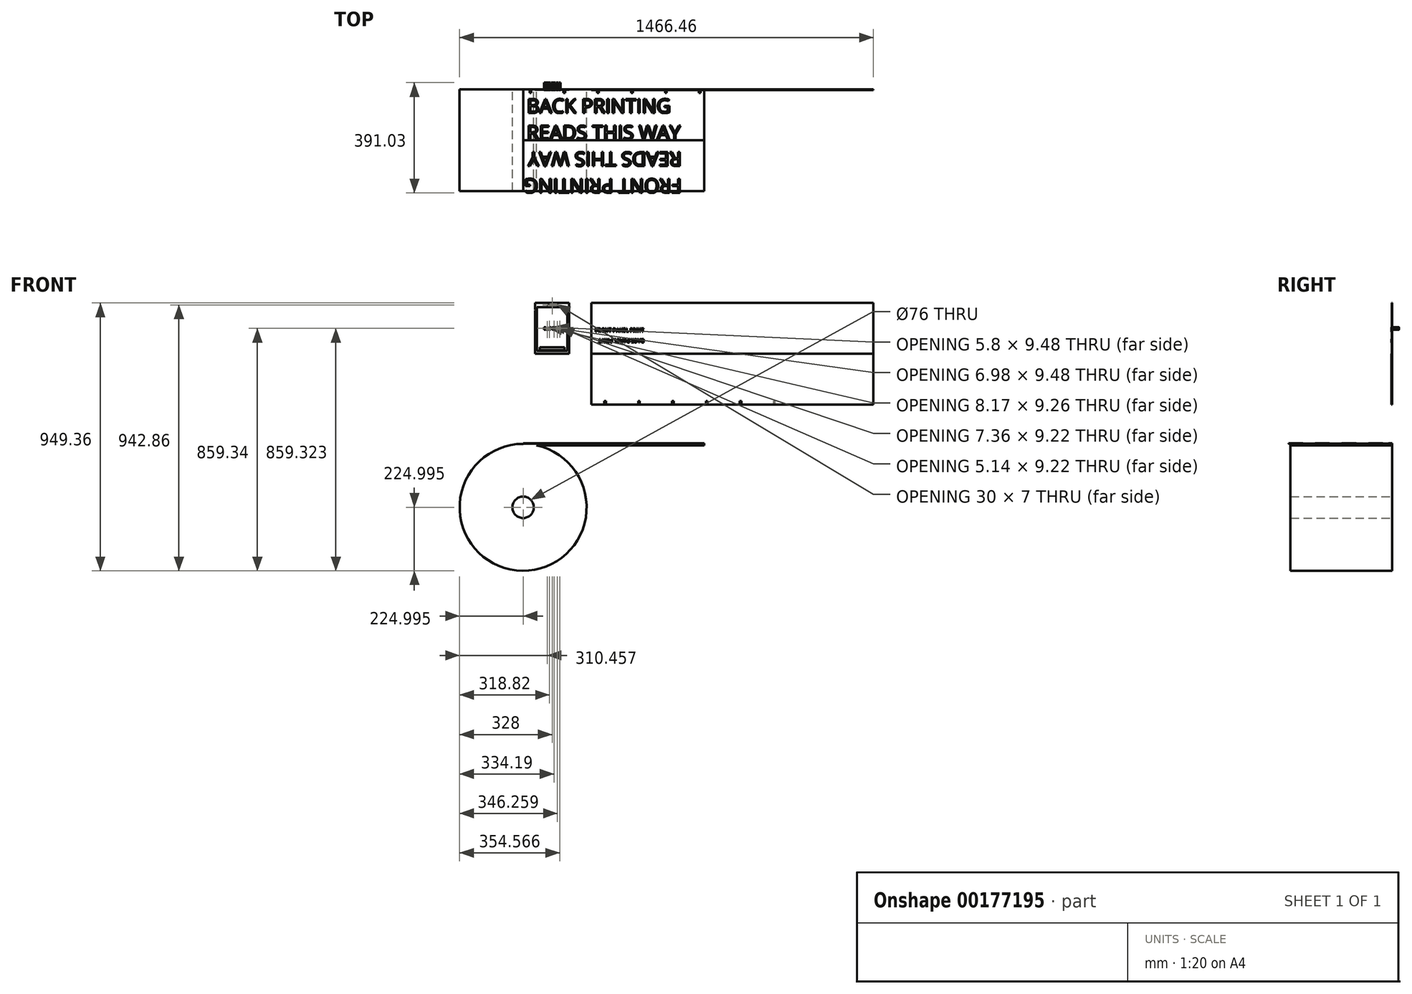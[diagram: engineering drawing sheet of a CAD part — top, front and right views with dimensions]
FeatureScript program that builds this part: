
annotation { "Feature Type Name" : "Feature", "Feature Type Description" : "" }
export const myFeature = defineFeature(function(context is Context, id is Id, definition is map)
    precondition{}
    {
        {
            assignVariable(context, id + "F0", {"name" : "hoogte", "anyValue" : 180});
        }
        {
            var Q0;
            Q0=qCreatedBy(makeId("Front.planeOp"),FACE);
            var sketch = newSketch(context, id + "F1", { "sketchPlane" : qUnion([Q0])});
            skLineSegment(sketch, "E0.bottom", {"start": v(-60, 90) * mm, "end": v(60, 90) * mm});
            skLineSegment(sketch, "E0.top", {"start": v(-60, -90) * mm, "end": v(60, -90) * mm});
            skLineSegment(sketch, "E0.left", {"start": v(-60, 90) * mm, "end": v(-60, -90) * mm});
            skLineSegment(sketch, "E0.right", {"start": v(60, 90) * mm, "end": v(60, -90) * mm});
            skLineSegment(sketch, "E1", {"start": v(-60, 66.41) * mm, "end": v(-58.59, 65) * mm});
            skLineSegment(sketch, "E2", {"start": v(-58.59, 65) * mm, "end": v(-60, 63.59) * mm});
            skLineSegment(sketch, "E3", {"start": v(60, 66.41) * mm, "end": v(58.59, 65) * mm});
            skLineSegment(sketch, "E4", {"start": v(58.59, 65) * mm, "end": v(60, 63.59) * mm});
            skLineSegment(sketch, "E5.bottom", {"start": v(138.46, 90) * mm, "end": v(1138.46, 90) * mm});
            skLineSegment(sketch, "E5.top", {"start": v(138.46, -270) * mm, "end": v(1138.46, -270) * mm});
            skLineSegment(sketch, "E5.left", {"start": v(138.46, 90) * mm, "end": v(138.46, -270) * mm});
            skLineSegment(sketch, "E5.right", {"start": v(1138.46, 90) * mm, "end": v(1138.46, -270) * mm});
            skLineSegment(sketch, "E6", {"start": v(138.46, -90) * mm, "end": v(1138.46, -90) * mm});
            skLineSegment(sketch, "E7", {"start": v(-60, 90) * mm, "end": v(60, -90) * mm, "construction": true});
            skLineSegment(sketch, "E8", {"start": v(60, 90) * mm, "end": v(-60, -90) * mm, "construction": true});
            skPoint(sketch, "E9", {"position": v(0, 0) * mm});
            skSolve(sketch);
        }
        {
            var Q0;
            {var subQ3=sQuery(id+"F1.wireOp",EDGE,"E0.bottom");Q0=makeQuery(id+"F1.imprint","IMPRINT",FACE,{"disambiguationData":[TD([[makeQuery(id+"F1.imprint","IMPRINT",EDGE,{"derivedFrom":subQ3}),-1.0]])]});}
            var Q1;
            Q1=makeQuery(id+"F1.imprint","IMPRINT",FACE,{"disambiguationData":[TD([[makeQuery(id+"F1.imprint","IMPRINT",EDGE,{"derivedFrom":sQuery(id+"F1.wireOp",EDGE,"E5.bottom")}),-1.0]])]});
            var Q2;
            {var subQ0=sQuery(id+"F1.wireOp",EDGE,"E5.top");Q2=makeQuery(id+"F1.imprint","IMPRINT",FACE,{"disambiguationData":[TD([[makeQuery(id+"F1.imprint","IMPRINT",EDGE,{"derivedFrom":subQ0}),1.0]])]});}
            extrude(context, id + "F2", {"entities" : qUnion([Q0, Q1, Q2]), "depth" : 1 * mm});
        }
        {
            var Q0;
            Q0=makeQuery(id+"F2.opExtrude","CAP_FACE",FACE,{"disambiguationData":[OSD([sQuery(id+"F1.wireOp",EDGE,"E0.bottom"),sQuery(id+"F1.wireOp",EDGE,"E0.top"),sQuery(id+"F1.wireOp",EDGE,"E0.left"),sQuery(id+"F1.wireOp",EDGE,"E0.right"),sQuery(id+"F1.wireOp",EDGE,"E1"),sQuery(id+"F1.wireOp",EDGE,"E2"),sQuery(id+"F1.wireOp",EDGE,"E3"),sQuery(id+"F1.wireOp",EDGE,"E4")])],"isStart":false});
            var sketch = newSketch(context, id + "F3", { "sketchPlane" : qUnion([Q0])});
            skLineSegment(sketch, "E10.0.0", {"start": v(60, 90) * mm, "end": v(-60, 90) * mm});
            skLineSegment(sketch, "E10.0.1", {"start": v(-60, 90) * mm, "end": v(-60, 66.41) * mm});
            skLineSegment(sketch, "E10.0.2", {"start": v(-60, 66.41) * mm, "end": v(-58.59, 65) * mm});
            skLineSegment(sketch, "E10.0.3", {"start": v(-58.59, 65) * mm, "end": v(-60, 63.59) * mm});
            skLineSegment(sketch, "E10.0.4", {"start": v(-60, 63.59) * mm, "end": v(-60, -90) * mm});
            skLineSegment(sketch, "E10.0.5", {"start": v(-60, -90) * mm, "end": v(60, -90) * mm});
            skLineSegment(sketch, "E10.0.6", {"start": v(60, -90) * mm, "end": v(60, 63.59) * mm});
            skLineSegment(sketch, "E10.0.7", {"start": v(60, 63.59) * mm, "end": v(58.59, 65) * mm});
            skLineSegment(sketch, "E10.0.8", {"start": v(58.59, 65) * mm, "end": v(60, 66.41) * mm});
            skLineSegment(sketch, "E10.0.9", {"start": v(60, 66.41) * mm, "end": v(60, 90) * mm});
            skLineSegment(sketch, "E11.bottom", {"start": v(-54, 75) * mm, "end": v(54, 75) * mm});
            skLineSegment(sketch, "E11.top", {"start": v(-54, -80) * mm, "end": v(54, -80) * mm});
            skLineSegment(sketch, "E11.left", {"start": v(-54, 75) * mm, "end": v(-54, -80) * mm});
            skLineSegment(sketch, "E11.right", {"start": v(54, 75) * mm, "end": v(54, -80) * mm});
            skLineSegment(sketch, "E12.bottom", {"start": v(-60, 90) * mm, "end": v(-57, 90) * mm});
            skLineSegment(sketch, "E12.top", {"start": v(-60, 78) * mm, "end": v(-57, 78) * mm});
            skLineSegment(sketch, "E12.left", {"start": v(-60, 90) * mm, "end": v(-60, 78) * mm});
            skLineSegment(sketch, "E12.right", {"start": v(-57, 90) * mm, "end": v(-57, 78) * mm});
            skLineSegment(sketch, "E13.bottom", {"start": v(60, 90) * mm, "end": v(57, 90) * mm});
            skLineSegment(sketch, "E13.top", {"start": v(60, 78) * mm, "end": v(57, 78) * mm});
            skLineSegment(sketch, "E13.left", {"start": v(60, 90) * mm, "end": v(60, 78) * mm});
            skLineSegment(sketch, "E13.right", {"start": v(57, 90) * mm, "end": v(57, 78) * mm});
            skLineSegment(sketch, "E14.bottom", {"start": v(-44, -67) * mm, "end": v(44, -67) * mm});
            skLineSegment(sketch, "E14.top", {"start": v(-44, -77) * mm, "end": v(44, -77) * mm});
            skLineSegment(sketch, "E14.left", {"start": v(-44, -67) * mm, "end": v(-44, -77) * mm});
            skLineSegment(sketch, "E14.right", {"start": v(44, -67) * mm, "end": v(44, -77) * mm});
            skSolve(sketch);
        }
        {
            var Q0;
            Q0=makeQuery(id+"F3.imprint","IMPRINT",FACE,{"disambiguationData":[TD([[makeQuery(id+"F3.imprint","IMPRINT",EDGE,{"derivedFrom":sQuery(id+"F3.wireOp",EDGE,"E11.bottom")}),-1.0]])]});
            var Q1;
            Q1=makeQuery(id+"F3.imprint","IMPRINT",FACE,{"disambiguationData":[TD([[makeQuery(id+"F3.imprint","IMPRINT",EDGE,{"derivedFrom":sQuery(id+"F3.wireOp",EDGE,"E12.bottom")}),-1.0]])]});
            var Q2;
            Q2=makeQuery(id+"F3.imprint","IMPRINT",FACE,{"disambiguationData":[TD([[makeQuery(id+"F3.imprint","IMPRINT",EDGE,{"derivedFrom":sQuery(id+"F3.wireOp",EDGE,"E13.bottom")}),-1.0]])]});
            extrude(context, id + "F4", {"entities" : qUnion([Q0, Q1, Q2]), "operationType" : NewBodyOperationType.REMOVE, "oppositeDirection" : true, "depth" : 0.5 * mm});
        }
        {
            var Q0;
            Q0=makeQuery(id+"F2.opExtrude","CAP_FACE",FACE,{"disambiguationData":[OSD([sQuery(id+"F1.wireOp",EDGE,"E5.bottom"),sQuery(id+"F1.wireOp",EDGE,"E5.left"),sQuery(id+"F1.wireOp",EDGE,"E5.right"),sQuery(id+"F1.wireOp",EDGE,"E6")])],"isStart":false});
            var sketch = newSketch(context, id + "F5", { "sketchPlane" : qUnion([Q0])});
            skLineSegment(sketch, "E15.0.0", {"start": v(1138.46, 90) * mm, "end": v(138.46, 90) * mm});
            skLineSegment(sketch, "E15.0.1", {"start": v(138.46, 90) * mm, "end": v(138.46, 90) * mm});
            skLineSegment(sketch, "E15.0.2", {"start": v(138.46, 90) * mm, "end": v(1138.46, 90) * mm});
            skLineSegment(sketch, "E15.0.3", {"start": v(1138.46, 90) * mm, "end": v(1138.46, 90) * mm});
            skLineSegment(sketch, "E16.bottom", {"start": v(184.68, -270) * mm, "end": v(190.68, -270) * mm});
            skLineSegment(sketch, "E16.top", {"start": v(184.68, -258) * mm, "end": v(190.68, -258) * mm});
            skLineSegment(sketch, "E16.left", {"start": v(184.68, -270) * mm, "end": v(184.68, -258) * mm});
            skLineSegment(sketch, "E16.right", {"start": v(190.68, -270) * mm, "end": v(190.68, -258) * mm});
            skLineSegment(sketch, "E17.1.0.0", {"start": v(304.68, -258) * mm, "end": v(310.68, -258) * mm});
            skLineSegment(sketch, "E17.1.0.1", {"start": v(304.68, -270) * mm, "end": v(304.68, -258) * mm});
            skLineSegment(sketch, "E17.1.0.2", {"start": v(304.68, -270) * mm, "end": v(310.68, -270) * mm});
            skLineSegment(sketch, "E17.1.0.3", {"start": v(310.68, -270) * mm, "end": v(310.68, -258) * mm});
            skLineSegment(sketch, "E17.2.0.0", {"start": v(424.68, -258) * mm, "end": v(430.68, -258) * mm});
            skLineSegment(sketch, "E17.2.0.1", {"start": v(424.68, -270) * mm, "end": v(424.68, -258) * mm});
            skLineSegment(sketch, "E17.2.0.2", {"start": v(424.68, -270) * mm, "end": v(430.68, -270) * mm});
            skLineSegment(sketch, "E17.2.0.3", {"start": v(430.68, -270) * mm, "end": v(430.68, -258) * mm});
            skLineSegment(sketch, "E17.direction1", {"start": v(184.68, -270) * mm, "end": v(304.68, -270) * mm, "construction": true});
            skLineSegment(sketch, "E18.0.3.0", {"start": v(544.68, -258) * mm, "end": v(550.68, -258) * mm});
            skLineSegment(sketch, "E18.3.3.0", {"start": v(544.68, -270) * mm, "end": v(544.68, -258) * mm});
            skLineSegment(sketch, "E18.6.3.0", {"start": v(544.68, -270) * mm, "end": v(550.68, -270) * mm});
            skLineSegment(sketch, "E18.9.3.0", {"start": v(550.68, -270) * mm, "end": v(550.68, -258) * mm});
            skLineSegment(sketch, "E18.0.4.0", {"start": v(664.68, -258) * mm, "end": v(670.68, -258) * mm});
            skLineSegment(sketch, "E18.3.4.0", {"start": v(664.68, -270) * mm, "end": v(664.68, -258) * mm});
            skLineSegment(sketch, "E18.6.4.0", {"start": v(664.68, -270) * mm, "end": v(670.68, -270) * mm});
            skLineSegment(sketch, "E18.9.4.0", {"start": v(670.68, -270) * mm, "end": v(670.68, -258) * mm});
            skLineSegment(sketch, "E19.0.5.0", {"start": v(784.68, -258) * mm, "end": v(790.68, -258) * mm});
            skLineSegment(sketch, "E19.3.5.0", {"start": v(784.68, -270) * mm, "end": v(784.68, -258) * mm});
            skLineSegment(sketch, "E19.6.5.0", {"start": v(784.68, -270) * mm, "end": v(790.68, -270) * mm});
            skLineSegment(sketch, "E19.9.5.0", {"start": v(790.68, -270) * mm, "end": v(790.68, -258) * mm});
            skSolve(sketch);
        }
        {
            var Q0;
            Q0=makeQuery(id+"F5.imprint","IMPRINT",FACE,{"disambiguationData":[TD([[makeQuery(id+"F5.imprint","IMPRINT",EDGE,{"derivedFrom":sQuery(id+"F5.wireOp",EDGE,"JLQzprwf-iRJq-cmRX-vWmS-HmgRmsplr5sc.top")}),-1.0]])]});
            var Q1;
            Q1=makeQuery(id+"F5.imprint","IMPRINT",FACE,{"disambiguationData":[TD([[makeQuery(id+"F5.imprint","IMPRINT",EDGE,{"derivedFrom":sQuery(id+"F5.wireOp",EDGE,"E16.bottom")}),1.0]])]});
            var Q2;
            Q2=makeQuery(id+"F5.imprint","IMPRINT",FACE,{"disambiguationData":[TD([[makeQuery(id+"F5.imprint","IMPRINT",EDGE,{"derivedFrom":sQuery(id+"F5.wireOp",EDGE,"E17.1.0.0")}),-1.0]])]});
            var Q3;
            Q3=makeQuery(id+"F5.imprint","IMPRINT",FACE,{"disambiguationData":[TD([[makeQuery(id+"F5.imprint","IMPRINT",EDGE,{"derivedFrom":sQuery(id+"F5.wireOp",EDGE,"E17.2.0.0")}),-1.0]])]});
            var Q4;
            Q4=makeQuery(id+"F5.imprint","IMPRINT",FACE,{"disambiguationData":[TD([[makeQuery(id+"F5.imprint","IMPRINT",EDGE,{"derivedFrom":sQuery(id+"F5.wireOp",EDGE,"E18.0.3.0")}),-1.0]])]});
            var Q5;
            Q5=makeQuery(id+"F5.imprint","IMPRINT",FACE,{"disambiguationData":[TD([[makeQuery(id+"F5.imprint","IMPRINT",EDGE,{"derivedFrom":sQuery(id+"F5.wireOp",EDGE,"E18.0.4.0")}),-1.0]])]});
            var Q6;
            Q6=makeQuery(id+"F5.imprint","IMPRINT",FACE,{"disambiguationData":[TD([[makeQuery(id+"F5.imprint","IMPRINT",EDGE,{"derivedFrom":sQuery(id+"F5.wireOp",EDGE,"E19.0.5.0")}),-1.0]])]});
            extrude(context, id + "F6", {"entities" : qUnion([Q0, Q1, Q2, Q3, Q4, Q5, Q6]), "operationType" : NewBodyOperationType.REMOVE, "oppositeDirection" : true, "depth" : 0.5 * mm});
        }
        {
            var Q0;
            Q0=qCreatedBy(makeId("Front.planeOp"),FACE);
            var sketch = newSketch(context, id + "F7", { "sketchPlane" : qUnion([Q0])});
            skCircle(sketch, "E20", {"center": v(-103, -634.36) * mm, "radius": 225 * mm});
            skLineSegment(sketch, "E21.bottom", {"start": v(-103, -408.35) * mm, "end": v(538.87, -408.35) * mm});
            skLineSegment(sketch, "E21.top", {"start": v(-103, -414.51) * mm, "end": v(538.87, -414.51) * mm});
            skLineSegment(sketch, "E21.left", {"start": v(-103, -414.51) * mm, "end": v(-103, -408.35) * mm});
            skLineSegment(sketch, "E21.right", {"start": v(538.87, -414.51) * mm, "end": v(538.87, -408.35) * mm});
            skCircle(sketch, "E22", {"center": v(-103, -634.36) * mm, "radius": 38 * mm});
            skSolve(sketch);
        }
        {
            var Q0;
            Q0=qSketchRegion(id+"F7",true);
            extrude(context, id + "F8", {"entities" : qUnion([Q0]), "depth" : (((getVariable(context, 'hoogte')) * 2)) * mm});
        }
        {
            var Q0;
            {var subQ0=sQuery(id+"F1.wireOp",EDGE,"E4");var subQ1=sQuery(id+"F1.wireOp",EDGE,"E2");var subQ2=sQuery(id+"F1.wireOp",EDGE,"E1");var subQ3=sQuery(id+"F1.wireOp",EDGE,"E0.right");var subQ4=sQuery(id+"F1.wireOp",EDGE,"E0.top");var subQ5=sQuery(id+"F1.wireOp",EDGE,"E0.bottom");var subQ6=sQuery(id+"F1.wireOp",EDGE,"E3");var subQ7=sQuery(id+"F1.wireOp",EDGE,"E0.left");Q0=makeQuery(id+"F4.boolean.opBoolean","SPLIT",FACE,{"disambiguationData":[TD([makeQuery(id+"F2.opExtrude","SWEPT_FACE",FACE,{"disambiguationData":[OSD([subQ5])]})])],"derivedFrom":makeQuery(id+"F2.opExtrude","CAP_FACE",FACE,{"disambiguationData":[OSD([subQ5,subQ4,subQ7,subQ3,subQ2,subQ1,subQ6,subQ0])],"isStart":false})});}
            var sketch = newSketch(context, id + "F9", { "sketchPlane" : qUnion([Q0])});
            skText(sketch, "E23", { "text": "BACKSIDE", "fontName": "OpenSans-Regular.ttf"});
            const initialGuessF9  = {"E23": [-0.03, -0.00465, 1, 0, 0.0093]};
            skSetInitialGuess(sketch, initialGuessF9);
            skSolve(sketch);
        }
        {
            var Q0;
            Q0=qSketchRegion(id+"F9",true);
            extrude(context, id + "F10", {"entities" : qUnion([Q0]), "operationType" : NewBodyOperationType.ADD, "depth" : 1 * mm, "hasSecondDirection" : true, "secondDirectionOppositeDirection" : true, "secondDirectionDepth" : 25 * mm});
        }
        {
            var Q0;
            {var subQ0=sQuery(id+"F1.wireOp",EDGE,"E5.bottom");var subQ1=sQuery(id+"F1.wireOp",EDGE,"E5.left");var subQ2=sQuery(id+"F1.wireOp",EDGE,"E5.right");Q0=makeQuery(id+"F6.boolean.opBoolean","SPLIT",FACE,{"disambiguationData":[TD([makeQuery(id+"F2.opExtrude","SWEPT_FACE",FACE,{"disambiguationData":[OSD([subQ0])]})])],"derivedFrom":makeQuery(id+"F2.opExtrude","CAP_FACE",FACE,{"disambiguationData":[OSD([subQ0,sQuery(id+"F1.wireOp",EDGE,"E5.top"),subQ1,subQ2])],"isStart":false})});}
            var sketch = newSketch(context, id + "F11", { "sketchPlane" : qUnion([Q0])});
            skText(sketch, "E24", { "text": "FRONT PANEL PRINT", "fontName": "AllertaStencil-Regular.ttf"});
            skLineSegment(sketch, "E25.0.0", {"start": v(1138.46, -90) * mm, "end": v(138.46, -90) * mm});
            skLineSegment(sketch, "E25.0.1", {"start": v(138.46, -90) * mm, "end": v(138.46, -270) * mm});
            skLineSegment(sketch, "E25.0.2", {"start": v(138.46, -270) * mm, "end": v(184.68, -270) * mm});
            skLineSegment(sketch, "E25.0.3", {"start": v(184.68, -270) * mm, "end": v(184.68, -258) * mm});
            skLineSegment(sketch, "E25.0.4", {"start": v(184.68, -258) * mm, "end": v(190.68, -258) * mm});
            skLineSegment(sketch, "E25.0.5", {"start": v(190.68, -258) * mm, "end": v(190.68, -270) * mm});
            skLineSegment(sketch, "E25.0.6", {"start": v(190.68, -270) * mm, "end": v(304.68, -270) * mm});
            skLineSegment(sketch, "E25.0.7", {"start": v(304.68, -270) * mm, "end": v(304.68, -258) * mm});
            skLineSegment(sketch, "E25.0.8", {"start": v(304.68, -258) * mm, "end": v(310.68, -258) * mm});
            skLineSegment(sketch, "E25.0.9", {"start": v(310.68, -258) * mm, "end": v(310.68, -270) * mm});
            skLineSegment(sketch, "E25.0.10", {"start": v(310.68, -270) * mm, "end": v(424.68, -270) * mm});
            skLineSegment(sketch, "E25.0.11", {"start": v(424.68, -270) * mm, "end": v(424.68, -258) * mm});
            skLineSegment(sketch, "E25.0.12", {"start": v(424.68, -258) * mm, "end": v(430.68, -258) * mm});
            skLineSegment(sketch, "E25.0.13", {"start": v(430.68, -258) * mm, "end": v(430.68, -270) * mm});
            skLineSegment(sketch, "E25.0.14", {"start": v(430.68, -270) * mm, "end": v(544.68, -270) * mm});
            skLineSegment(sketch, "E25.0.15", {"start": v(544.68, -270) * mm, "end": v(544.68, -258) * mm});
            skLineSegment(sketch, "E25.0.16", {"start": v(544.68, -258) * mm, "end": v(550.68, -258) * mm});
            skLineSegment(sketch, "E25.0.17", {"start": v(550.68, -258) * mm, "end": v(550.68, -270) * mm});
            skLineSegment(sketch, "E25.0.18", {"start": v(550.68, -270) * mm, "end": v(664.68, -270) * mm});
            skLineSegment(sketch, "E25.0.19", {"start": v(664.68, -270) * mm, "end": v(664.68, -258) * mm});
            skLineSegment(sketch, "E25.0.20", {"start": v(664.68, -258) * mm, "end": v(670.68, -258) * mm});
            skLineSegment(sketch, "E25.0.21", {"start": v(670.68, -258) * mm, "end": v(670.68, -270) * mm});
            skLineSegment(sketch, "E25.0.22", {"start": v(670.68, -270) * mm, "end": v(1138.46, -270) * mm});
            skLineSegment(sketch, "E25.0.23", {"start": v(1138.46, -270) * mm, "end": v(1138.46, -90) * mm});
            skText(sketch, "E26", { "text": "BACK PANEL PRINT", "fontName": "AllertaStencil-Regular.ttf"});
            skLineSegment(sketch, "E27", {"start": v(1093.46, -180) * mm, "end": v(1093.46, -181.37) * mm});
            const initialGuessF11  = {"E24": [0.1529, -0.0125, 1, 0, 0.0125], "E26": [0.32596, -0.0375, -1, 0, 0.0125]};
            skSetInitialGuess(sketch, initialGuessF11);
            skSolve(sketch);
        }
        {
            var Q0;
            Q0=qSketchRegion(id+"F11",true);
            extrude(context, id + "F12", {"entities" : qUnion([Q0]), "operationType" : NewBodyOperationType.ADD, "depth" : 1 * mm});
        }
        {
            var Q0;
            Q0=makeQuery(id+"F8.opExtrude","SWEPT_FACE",FACE,{"disambiguationData":[OSD([sQuery(id+"F7.wireOp",EDGE,"E21.bottom")])]});
            var sketch = newSketch(context, id + "F13", { "sketchPlane" : qUnion([Q0])});
            skText(sketch, "E28", { "text": "BACK PRINTING \nREADS THIS WAY", "fontName": "OpenSans-Regular.ttf"});
            skText(sketch, "E29", { "text": "FRONT PRINTING\nREADS THIS WAY", "fontName": "OpenSans-Regular.ttf"});
            skLineSegment(sketch, "E30", {"start": v(466.87, -267.44) * mm, "end": v(466.87, -330) * mm});
            skLineSegment(sketch, "E31", {"start": v(538.87, -180) * mm, "end": v(-103, -180) * mm, "construction": true});
            skLineSegment(sketch, "E32.bottom", {"start": v(538.87, -180) * mm, "end": v(-103, -180) * mm});
            skLineSegment(sketch, "E32.top", {"start": v(538.87, -179.95) * mm, "end": v(-103, -179.95) * mm});
            skLineSegment(sketch, "E32.left", {"start": v(538.87, -180) * mm, "end": v(538.87, -179.95) * mm});
            skLineSegment(sketch, "E32.right", {"start": v(-103, -180) * mm, "end": v(-103, -179.95) * mm});
            skLineSegment(sketch, "E33.bottom", {"start": v(538.87, -180.05) * mm, "end": v(-103, -180.05) * mm});
            skLineSegment(sketch, "E33.left", {"start": v(538.87, -180.05) * mm, "end": v(538.87, -180) * mm});
            skLineSegment(sketch, "E33.right", {"start": v(-103, -180.05) * mm, "end": v(-103, -180) * mm});
            skLineSegment(sketch, "E34.bottom", {"start": v(-80.23, 0) * mm, "end": v(-74.23, 0) * mm});
            skLineSegment(sketch, "E34.top", {"start": v(-80.23, -12) * mm, "end": v(-74.23, -12) * mm});
            skLineSegment(sketch, "E34.left", {"start": v(-80.23, 0) * mm, "end": v(-80.23, -12) * mm});
            skLineSegment(sketch, "E34.right", {"start": v(-74.23, 0) * mm, "end": v(-74.23, -12) * mm});
            skLineSegment(sketch, "E35.1.0.0", {"start": v(39.77, 0) * mm, "end": v(45.77, 0) * mm});
            skLineSegment(sketch, "E35.1.0.1", {"start": v(39.77, -12) * mm, "end": v(45.77, -12) * mm});
            skLineSegment(sketch, "E35.1.0.2", {"start": v(39.77, 0) * mm, "end": v(39.77, -12) * mm});
            skLineSegment(sketch, "E35.1.0.3", {"start": v(45.77, 0) * mm, "end": v(45.77, -12) * mm});
            skLineSegment(sketch, "E35.2.0.0", {"start": v(159.77, 0) * mm, "end": v(165.77, 0) * mm});
            skLineSegment(sketch, "E35.2.0.1", {"start": v(159.77, -12) * mm, "end": v(165.77, -12) * mm});
            skLineSegment(sketch, "E35.2.0.2", {"start": v(159.77, 0) * mm, "end": v(159.77, -12) * mm});
            skLineSegment(sketch, "E35.2.0.3", {"start": v(165.77, 0) * mm, "end": v(165.77, -12) * mm});
            skLineSegment(sketch, "E35.direction1", {"start": v(-80.23, -12) * mm, "end": v(39.77, -12) * mm, "construction": true});
            skLineSegment(sketch, "E36.0.3.0", {"start": v(279.77, 0) * mm, "end": v(285.77, 0) * mm});
            skLineSegment(sketch, "E36.3.3.0", {"start": v(279.77, -12) * mm, "end": v(285.77, -12) * mm});
            skLineSegment(sketch, "E36.6.3.0", {"start": v(279.77, 0) * mm, "end": v(279.77, -12) * mm});
            skLineSegment(sketch, "E36.9.3.0", {"start": v(285.77, 0) * mm, "end": v(285.77, -12) * mm});
            skLineSegment(sketch, "E36.0.4.0", {"start": v(399.77, 0) * mm, "end": v(405.77, 0) * mm});
            skLineSegment(sketch, "E36.3.4.0", {"start": v(399.77, -12) * mm, "end": v(405.77, -12) * mm});
            skLineSegment(sketch, "E36.6.4.0", {"start": v(399.77, 0) * mm, "end": v(399.77, -12) * mm});
            skLineSegment(sketch, "E36.9.4.0", {"start": v(405.77, 0) * mm, "end": v(405.77, -12) * mm});
            skLineSegment(sketch, "E36.0.5.0", {"start": v(519.77, 0) * mm, "end": v(525.77, 0) * mm});
            skLineSegment(sketch, "E36.3.5.0", {"start": v(519.77, -12) * mm, "end": v(525.77, -12) * mm});
            skLineSegment(sketch, "E36.6.5.0", {"start": v(519.77, 0) * mm, "end": v(519.77, -12) * mm});
            skLineSegment(sketch, "E36.9.5.0", {"start": v(525.77, 0) * mm, "end": v(525.77, -12) * mm});
            const initialGuessF13  = {"E28": [-0.09022, -0.08333, 1, 0, 0.05], "E29": [0.45887, -0.31667, -1, 0, 0.05]};
            skSetInitialGuess(sketch, initialGuessF13);
            skSolve(sketch);
        }
        {
            var Q0;
            Q0=qSketchRegion(id+"F13",true);
            extrude(context, id + "F14", {"entities" : qUnion([Q0]), "operationType" : NewBodyOperationType.ADD, "depth" : 1 * mm});
        }
        {
            var Q0;
            {var subQ0=sQuery(id+"F1.wireOp",EDGE,"E4");var subQ1=sQuery(id+"F1.wireOp",EDGE,"E2");var subQ2=sQuery(id+"F1.wireOp",EDGE,"E1");var subQ3=sQuery(id+"F1.wireOp",EDGE,"E0.right");var subQ4=sQuery(id+"F1.wireOp",EDGE,"E0.top");var subQ5=sQuery(id+"F1.wireOp",EDGE,"E0.bottom");var subQ6=sQuery(id+"F1.wireOp",EDGE,"E3");var subQ7=sQuery(id+"F1.wireOp",EDGE,"E0.left");Q0=makeQuery(id+"F4.boolean.opBoolean","SPLIT",FACE,{"disambiguationData":[TD([makeQuery(id+"F2.opExtrude","SWEPT_FACE",FACE,{"disambiguationData":[OSD([subQ5])]})])],"derivedFrom":makeQuery(id+"F2.opExtrude","CAP_FACE",FACE,{"disambiguationData":[OSD([subQ5,subQ4,subQ7,subQ3,subQ2,subQ1,subQ6,subQ0])],"isStart":false})});}
            var sketch = newSketch(context, id + "F15", { "sketchPlane" : qUnion([Q0])});
            skLineSegment(sketch, "E37.0.0", {"start": v(-57, 78) * mm, "end": v(-60, 78) * mm});
            skLineSegment(sketch, "E37.0.1", {"start": v(-60, 78) * mm, "end": v(-60, 66.41) * mm});
            skLineSegment(sketch, "E37.0.2", {"start": v(-60, 66.41) * mm, "end": v(-58.59, 65) * mm});
            skLineSegment(sketch, "E37.0.3", {"start": v(-58.59, 65) * mm, "end": v(-60, 63.59) * mm});
            skLineSegment(sketch, "E37.0.4", {"start": v(-60, 63.59) * mm, "end": v(-60, -90) * mm});
            skLineSegment(sketch, "E37.0.5", {"start": v(-60, -90) * mm, "end": v(60, -90) * mm});
            skLineSegment(sketch, "E37.0.6", {"start": v(60, -90) * mm, "end": v(60, 63.59) * mm});
            skLineSegment(sketch, "E37.0.7", {"start": v(60, 63.59) * mm, "end": v(58.59, 65) * mm});
            skLineSegment(sketch, "E37.0.8", {"start": v(58.59, 65) * mm, "end": v(60, 66.41) * mm});
            skLineSegment(sketch, "E37.0.9", {"start": v(60, 66.41) * mm, "end": v(60, 78) * mm});
            skLineSegment(sketch, "E37.0.10", {"start": v(60, 78) * mm, "end": v(57, 78) * mm});
            skLineSegment(sketch, "E37.0.11", {"start": v(57, 78) * mm, "end": v(57, 90) * mm});
            skLineSegment(sketch, "E37.0.12", {"start": v(57, 90) * mm, "end": v(-57, 90) * mm});
            skLineSegment(sketch, "E37.0.13", {"start": v(-57, 90) * mm, "end": v(-57, 78) * mm});
            skLineSegment(sketch, "E38.bottom", {"start": v(-13, 84) * mm, "end": v(13, 84) * mm});
            skLineSegment(sketch, "E38.top", {"start": v(-13, 80) * mm, "end": v(13, 80) * mm});
            skLineSegment(sketch, "E38.left", {"start": v(-13, 84) * mm, "end": v(-13, 80) * mm});
            skLineSegment(sketch, "E38.right", {"start": v(13, 84) * mm, "end": v(13, 80) * mm});
            skCircle(sketch, "E39", {"center": v(-13, 82) * mm, "radius": 2 * mm});
            skCircle(sketch, "E40", {"center": v(13, 82) * mm, "radius": 2 * mm});
            skCircle(sketch, "E41", {"center": v(0, 84) * mm, "radius": 3 * mm});
            skLineSegment(sketch, "E42", {"start": v(0, 90) * mm, "end": v(0, 75) * mm, "construction": true});
            skSolve(sketch);
        }
        {
            var Q0;
            {var subQ0=sQuery(id+"F15.wireOp",EDGE,"E41");var subQ1=sQuery(id+"F15.wireOp",EDGE,"E38.bottom");var subQ2=makeQuery(id+"F15.imprint","INTERSECT",VERTEX,{"disambiguationData":[OD(0.0)],"derivedFrom":[subQ1,subQ0]});Q0=makeQuery(id+"F15.imprint","IMPRINT",FACE,{"disambiguationData":[TD([[makeQuery(id+"F15.imprint","IMPRINT",EDGE,{"disambiguationData":[TD([[subQ2,-1.0]])],"derivedFrom":subQ1}),-1.0]])]});}
            var Q1;
            {var subQ0=sQuery(id+"F15.wireOp",EDGE,"E41");var subQ1=sQuery(id+"F15.wireOp",EDGE,"E38.bottom");var subQ2=makeQuery(id+"F15.imprint","INTERSECT",VERTEX,{"disambiguationData":[OD(0.0)],"derivedFrom":[subQ1,subQ0]});Q1=makeQuery(id+"F15.imprint","IMPRINT",FACE,{"disambiguationData":[TD([[makeQuery(id+"F15.imprint","IMPRINT",EDGE,{"disambiguationData":[TD([[subQ2,-1.0]])],"derivedFrom":subQ1}),1.0]])]});}
            var Q2;
            {var subQ4=sQuery(id+"F15.wireOp",EDGE,"E38.top");Q2=makeQuery(id+"F15.imprint","IMPRINT",FACE,{"disambiguationData":[TD([[makeQuery(id+"F15.imprint","IMPRINT",EDGE,{"derivedFrom":subQ4}),1.0]])]});}
            var Q3;
            {var subQ0=sQuery(id+"F15.wireOp",EDGE,"E38.left");Q3=makeQuery(id+"F15.imprint","IMPRINT",FACE,{"disambiguationData":[TD([[makeQuery(id+"F15.imprint","IMPRINT",EDGE,{"derivedFrom":subQ0}),1.0]])]});}
            var Q4;
            {var subQ0=sQuery(id+"F15.wireOp",EDGE,"E38.left");Q4=makeQuery(id+"F15.imprint","IMPRINT",FACE,{"disambiguationData":[TD([[makeQuery(id+"F15.imprint","IMPRINT",EDGE,{"derivedFrom":subQ0}),-1.0]])]});}
            var Q5;
            {var subQ0=sQuery(id+"F15.wireOp",EDGE,"E38.right");Q5=makeQuery(id+"F15.imprint","IMPRINT",FACE,{"disambiguationData":[TD([[makeQuery(id+"F15.imprint","IMPRINT",EDGE,{"derivedFrom":subQ0}),-1.0]])]});}
            var Q6;
            {var subQ0=sQuery(id+"F15.wireOp",EDGE,"E38.right");Q6=makeQuery(id+"F15.imprint","IMPRINT",FACE,{"disambiguationData":[TD([[makeQuery(id+"F15.imprint","IMPRINT",EDGE,{"derivedFrom":subQ0}),1.0]])]});}
            extrude(context, id + "F16", {"entities" : qUnion([Q0, Q1, Q2, Q3, Q4, Q5, Q6]), "operationType" : NewBodyOperationType.REMOVE, "oppositeDirection" : true, "depth" : 25 * mm});
        }
    });
